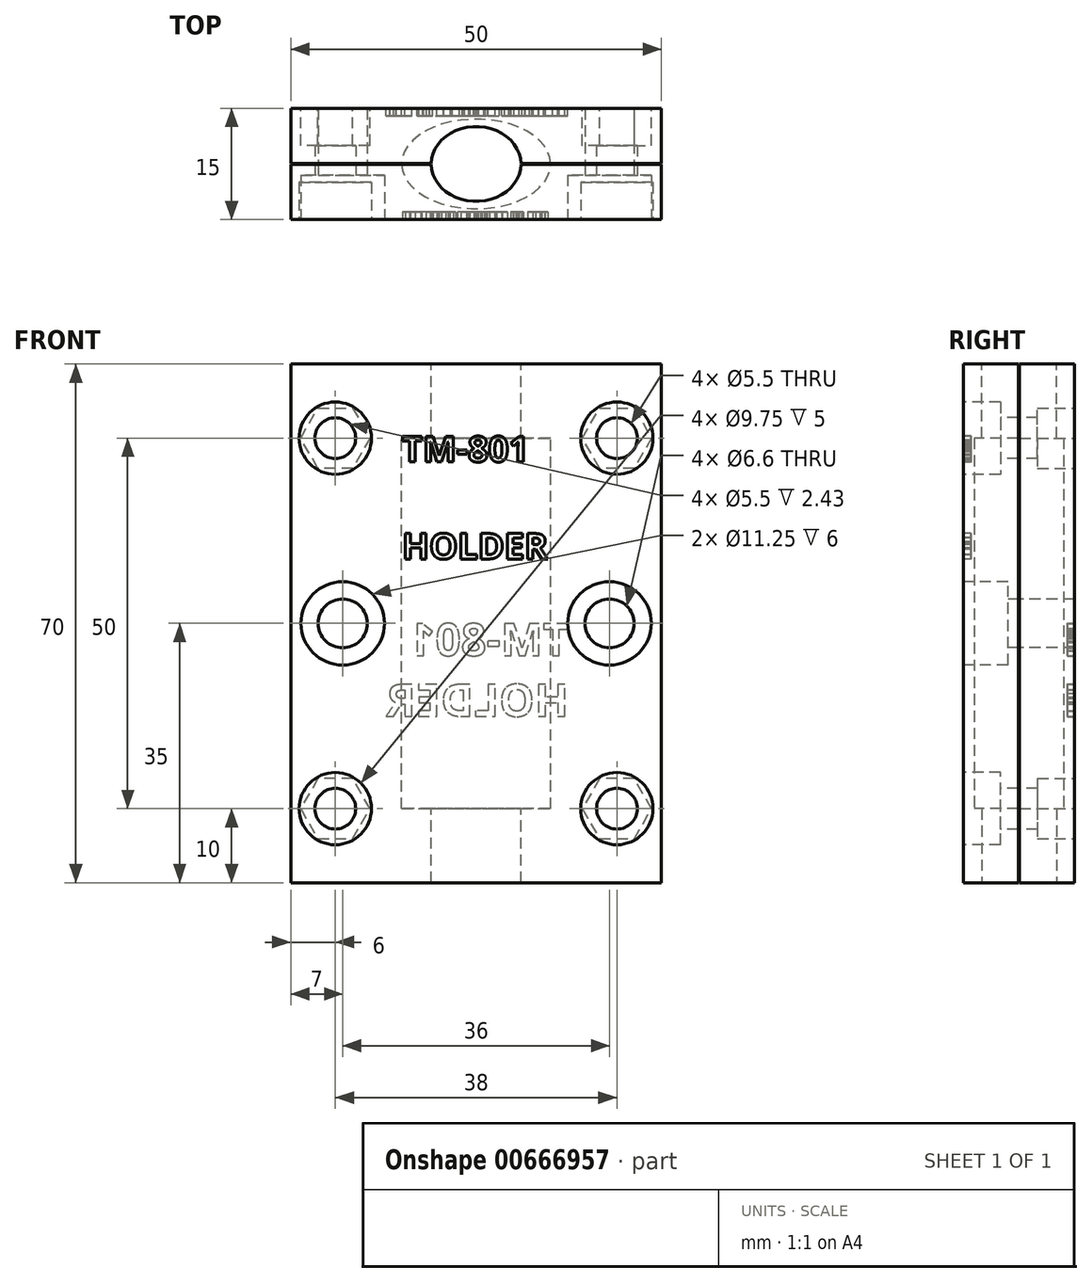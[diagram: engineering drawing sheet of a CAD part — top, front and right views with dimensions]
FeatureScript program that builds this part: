
annotation { "Feature Type Name" : "Feature", "Feature Type Description" : "" }
export const myFeature = defineFeature(function(context is Context, id is Id, definition is map)
    precondition{}
    {
        {
            var Q0;
            Q0=qCreatedBy(makeId("Top.planeOp"),FACE);
            var sketch = newSketch(context, id + "F0", { "sketchPlane" : qUnion([Q0])});
            skEllipse(sketch, "E0", {"center": v(0, 0) * mm, "majorRadius": 10.05 * mm, "minorRadius": 6.05 * mm, "majorAxis": v(-1, 0)});
            skSolve(sketch);
        }
        {
            var Q0;
            Q0=makeQuery(id+"F0.imprint","IMPRINT",FACE,{"disambiguationData":[TD([[makeQuery(id+"F0.imprint","IMPRINT",EDGE,{"derivedFrom":sQuery(id+"F0.wireOp",EDGE,"E0")}),1.0]])]});
            var sketch = newSketch(context, id + "F1", { "sketchPlane" : qUnion([Q0])});
            skEllipse(sketch, "E1", {"center": v(0, 0) * mm, "majorRadius": 6.05 * mm, "minorRadius": 5.05 * mm, "majorAxis": v(-1, 0)});
            skSolve(sketch);
        }
        {
            var Q0;
            Q0=qCreatedBy(makeId("Top.planeOp"),FACE);
            var sketch = newSketch(context, id + "F2", { "sketchPlane" : qUnion([Q0])});
            skLineSegment(sketch, "E2.bottom", {"start": v(-25, -7.5) * mm, "end": v(25, -7.5) * mm});
            skLineSegment(sketch, "E2.top", {"start": v(-25, 7.5) * mm, "end": v(25, 7.5) * mm});
            skLineSegment(sketch, "E2.left", {"start": v(-25, -7.5) * mm, "end": v(-25, 7.5) * mm});
            skLineSegment(sketch, "E2.right", {"start": v(25, -7.5) * mm, "end": v(25, 7.5) * mm});
            skPoint(sketch, "E2.middle", {"position": v(0, 0) * mm});
            skSolve(sketch);
        }
        {
            var Q0;
            Q0 = qSketchRegion(id + "F2", true);
            extrude(context, id + "F3", {"entities" : qUnion([Q0]), "oppositeDirection" : true, "depth" : 35 * mm, "offsetDistance" : 25 * mm});
        }
        {
            var Q0;
            Q0=makeQuery(id+"F1.imprint","IMPRINT",FACE,{"disambiguationData":[TD([[makeQuery(id+"F1.imprint","IMPRINT",EDGE,{"derivedFrom":sQuery(id+"F1.wireOp",EDGE,"E1")}),1.0]])]});
            var Q1;
            Q1=sQuery(id+"F1.wireOp",EDGE,"E1");
            extrude(context, id + "F4", {"entities" : qUnion([Q0]), "operationType" : NewBodyOperationType.REMOVE, "surfaceEntities" : qUnion([Q1]), "endBound" : BoundingType.THROUGH_ALL, "oppositeDirection" : true, "depth" : 25 * mm, "offsetDistance" : 25 * mm});
        }
        {
            var Q0;
            Q0 = qSketchRegion(id + "F0", true);
            var Q1;
            Q1=sQuery(id+"F0.wireOp",EDGE,"E0");
            extrude(context, id + "F5", {"entities" : qUnion([Q0]), "operationType" : NewBodyOperationType.REMOVE, "surfaceEntities" : qUnion([Q1]), "oppositeDirection" : true, "depth" : 25 * mm, "offsetDistance" : 25 * mm});
        }
        {
            var Q0;
            Q0=makeQuery(id+"F3.opExtrude","SWEPT_FACE",FACE,{"disambiguationData":[OSD([sQuery(id+"F2.wireOp",EDGE,"E2.bottom")])]});
            var sketch = newSketch(context, id + "F6", { "sketchPlane" : qUnion([Q0])});
            skPoint(sketch, "E3", {"position": v(-19, -25) * mm});
            skPoint(sketch, "E4", {"position": v(19, -25) * mm});
            skSolve(sketch);
        }
        {
            var Q0;
            Q0=sQuery(id+"F6.wireOp",VERTEX,"E3");
            var Q1;
            Q1=sQuery(id+"F6.wireOp",VERTEX,"E4");
            var Q2;
            Q2=makeQuery(id+"F3.opExtrude","SWEPT_BODY",BODY,{"disambiguationData":[OSD([sQuery(id+"F2.wireOp",EDGE,"E2.bottom"),sQuery(id+"F2.wireOp",EDGE,"E2.top"),sQuery(id+"F2.wireOp",EDGE,"E2.left"),sQuery(id+"F2.wireOp",EDGE,"E2.right")])]});
            hole(context, id + "F7", {"style" : HoleStyle.C_BORE, "endStyle" : HoleEndStyle.THROUGH, "standardTappedOrClearance" : lookupTablePath({ "standard" : "ISO", "fit" : "Normal", "size" : "M5", "type" : "Clearance" }), "standardBlindInLast" : lookupTablePath({ "fit" : "Standard", "standard" : "ISO", "size" : "M5", "type" : "Clearance" }), "holeDiameter" : 5.5 * mm, "cBoreDiameter" : 9.75 * mm, "cBoreDepth" : 5 * mm, "majorDiameter" : 5 * mm, "isTappedThrough" : true, "tappedDepth" : 12 * mm, "tapClearance" : 3, "startFromSketch" : true, "locations" : qUnion([Q0, Q1]), "scope" : qUnion([Q2])});
        }
        {
            var Q0;
            Q0=makeQuery(id+"F3.opExtrude","SWEPT_FACE",FACE,{"disambiguationData":[OSD([sQuery(id+"F2.wireOp",EDGE,"E2.top")])]});
            var sketch = newSketch(context, id + "F8", { "sketchPlane" : qUnion([Q0])});
            skCircle(sketch, "E5.cCircle", {"center": v(-19, -25) * mm, "radius": 4.05 * mm, "construction": true});
            skLineSegment(sketch, "E5.0", {"start": v(-16.66, -29.05) * mm, "end": v(-21.34, -29.05) * mm});
            skLineSegment(sketch, "E5.1", {"start": v(-21.34, -29.05) * mm, "end": v(-23.68, -25) * mm});
            skLineSegment(sketch, "E5.2", {"start": v(-23.68, -25) * mm, "end": v(-21.34, -20.95) * mm});
            skLineSegment(sketch, "E5.3", {"start": v(-21.34, -20.95) * mm, "end": v(-16.66, -20.95) * mm});
            skLineSegment(sketch, "E5.4", {"start": v(-16.66, -20.95) * mm, "end": v(-14.32, -25) * mm});
            skLineSegment(sketch, "E5.5", {"start": v(-14.32, -25) * mm, "end": v(-16.66, -29.05) * mm});
            skPoint(sketch, "E5.0.midPoint", {"position": v(-19, -29.05) * mm});
            skPoint(sketch, "E6.0.midPoint", {"position": v(-22.5, -27.03) * mm});
            skCircle(sketch, "E7.cCircle", {"center": v(19, -25) * mm, "radius": 4.05 * mm, "construction": true});
            skLineSegment(sketch, "E7.0", {"start": v(16.66, -29.05) * mm, "end": v(14.32, -25) * mm});
            skLineSegment(sketch, "E7.1", {"start": v(14.32, -25) * mm, "end": v(16.66, -20.95) * mm});
            skLineSegment(sketch, "E7.2", {"start": v(16.66, -20.95) * mm, "end": v(21.34, -20.95) * mm});
            skLineSegment(sketch, "E7.3", {"start": v(21.34, -20.95) * mm, "end": v(23.68, -25) * mm});
            skLineSegment(sketch, "E7.4", {"start": v(23.68, -25) * mm, "end": v(21.34, -29.05) * mm});
            skLineSegment(sketch, "E7.5", {"start": v(21.34, -29.05) * mm, "end": v(16.66, -29.05) * mm});
            skPoint(sketch, "E7.0.midPoint", {"position": v(15.5, -27.03) * mm});
            skSolve(sketch);
        }
        {
            var Q0;
            Q0=makeQuery(id+"F8.imprint","IMPRINT",FACE,{"disambiguationData":[TD([[makeQuery(id+"F8.imprint","IMPRINT",EDGE,{"derivedFrom":sQuery(id+"F8.wireOp",EDGE,"E5.1")}),-1.0]])]});
            extrude(context, id + "F9", {"entities" : qUnion([Q0]), "operationType" : NewBodyOperationType.REMOVE, "oppositeDirection" : true, "depth" : 5 * mm, "offsetDistance" : 25 * mm});
        }
        {
            var Q0;
            Q0 = qSketchRegion(id + "F8", true);
            extrude(context, id + "F10", {"entities" : qUnion([Q0]), "operationType" : NewBodyOperationType.REMOVE, "oppositeDirection" : true, "depth" : 5 * mm, "offsetDistance" : 25 * mm});
        }
        {
            var Q0;
            Q0=makeQuery(id+"F3.opExtrude","SWEPT_BODY",BODY,{"disambiguationData":[OSD([sQuery(id+"F2.wireOp",EDGE,"E2.bottom"),sQuery(id+"F2.wireOp",EDGE,"E2.top"),sQuery(id+"F2.wireOp",EDGE,"E2.left"),sQuery(id+"F2.wireOp",EDGE,"E2.right")])]});
            var Q1;
            Q1=makeQuery(id+"F2.imprint","IMPRINT",FACE,{"disambiguationData":[TD([[makeQuery(id+"F2.imprint","IMPRINT",EDGE,{"derivedFrom":sQuery(id+"F2.wireOp",EDGE,"E2.bottom")}),1.0]])]});
            mirror(context, id + "F11", {"operationType" : NewBodyOperationType.ADD, "entities" : qUnion([Q0]), "mirrorPlane" : qUnion([Q1])});
        }
        {
            var Q0;
            {var subQ0=makeQuery(id+"F3.opExtrude","SWEPT_FACE",FACE,{"disambiguationData":[OSD([sQuery(id+"F2.wireOp",EDGE,"E2.bottom")])]});Q0=makeQuery(id+"F11.boolean.opBoolean","MERGE",FACE,{"derivedFrom":[subQ0,makeQuery(id+"F11.opPattern","COPY",FACE,{"derivedFrom":subQ0,"instanceName":"1"})]});}
            var sketch = newSketch(context, id + "F12", { "sketchPlane" : qUnion([Q0])});
            skPoint(sketch, "E8", {"position": v(-18, 0) * mm});
            skPoint(sketch, "E9", {"position": v(18, 0) * mm});
            skSolve(sketch);
        }
        {
            var Q0;
            Q0=sQuery(id+"F12.wireOp",VERTEX,"E8");
            var Q1;
            Q1=sQuery(id+"F12.wireOp",VERTEX,"E9");
            var Q2;
            Q2=makeQuery(id+"F3.opExtrude","SWEPT_BODY",BODY,{"disambiguationData":[OSD([sQuery(id+"F2.wireOp",EDGE,"E2.bottom"),sQuery(id+"F2.wireOp",EDGE,"E2.top"),sQuery(id+"F2.wireOp",EDGE,"E2.left"),sQuery(id+"F2.wireOp",EDGE,"E2.right")])]});
            hole(context, id + "F13", {"style" : HoleStyle.C_BORE, "endStyle" : HoleEndStyle.THROUGH, "standardTappedOrClearance" : lookupTablePath({ "standard" : "ISO", "fit" : "Normal", "size" : "M6", "type" : "Clearance" }), "standardBlindInLast" : lookupTablePath({ "fit" : "Standard", "standard" : "ISO", "size" : "M6", "type" : "Clearance" }), "holeDiameter" : 6.6 * mm, "cBoreDiameter" : 11.25 * mm, "cBoreDepth" : 6 * mm, "majorDiameter" : 5 * mm, "isTappedThrough" : true, "tappedDepth" : 12 * mm, "tapClearance" : 3, "startFromSketch" : true, "locations" : qUnion([Q0, Q1]), "scope" : qUnion([Q2])});
        }
        {
            var Q0;
            Q0=makeQuery(id+"F11.opPattern","COPY",FACE,{"derivedFrom":makeQuery(id+"F3.opExtrude","CAP_FACE",FACE,{"disambiguationData":[OSD([sQuery(id+"F2.wireOp",EDGE,"E2.bottom"),sQuery(id+"F2.wireOp",EDGE,"E2.top"),sQuery(id+"F2.wireOp",EDGE,"E2.left"),sQuery(id+"F2.wireOp",EDGE,"E2.right")])],"isStart":false}),"instanceName":"1"});
            var sketch = newSketch(context, id + "F14", { "sketchPlane" : qUnion([Q0])});
            skLineSegment(sketch, "E10.bottom", {"start": v(-25, -0.08) * mm, "end": v(25, -0.08) * mm});
            skLineSegment(sketch, "E10.top", {"start": v(-25, 0.07) * mm, "end": v(25, 0.07) * mm});
            skLineSegment(sketch, "E10.left", {"start": v(-25, -0.07) * mm, "end": v(-25, 0.08) * mm});
            skLineSegment(sketch, "E10.right", {"start": v(25, -0.07) * mm, "end": v(25, 0.08) * mm});
            skPoint(sketch, "E10.middle", {"position": v(0, 0) * mm});
            skSolve(sketch);
        }
        {
            var Q0;
            {var subQ0=sQuery(id+"F14.wireOp",EDGE,"E10.left");Q0=makeQuery(id+"F14.imprint","IMPRINT",FACE,{"disambiguationData":[TD([[makeQuery(id+"F14.imprint","IMPRINT",EDGE,{"derivedFrom":subQ0}),-1.0]])]});}
            var Q1;
            {var subQ0=sQuery(id+"F14.wireOp",EDGE,"E10.right");Q1=makeQuery(id+"F14.imprint","IMPRINT",FACE,{"disambiguationData":[TD([[makeQuery(id+"F14.imprint","IMPRINT",EDGE,{"derivedFrom":subQ0}),1.0]])]});}
            extrude(context, id + "F15", {"entities" : qUnion([Q0, Q1]), "operationType" : NewBodyOperationType.REMOVE, "endBound" : BoundingType.THROUGH_ALL, "oppositeDirection" : true, "depth" : 25 * mm, "offsetDistance" : 25 * mm});
        }
        {
            var Q0;
            {var subQ0=makeQuery(id+"F3.opExtrude","SWEPT_FACE",FACE,{"disambiguationData":[OSD([sQuery(id+"F2.wireOp",EDGE,"E2.bottom")])]});Q0=makeQuery(id+"F11.boolean.opBoolean","MERGE",FACE,{"derivedFrom":[subQ0,makeQuery(id+"F11.opPattern","COPY",FACE,{"derivedFrom":subQ0,"instanceName":"1"})]});}
            var sketch = newSketch(context, id + "F16", { "sketchPlane" : qUnion([Q0])});
            skText(sketch, "E11", { "text": "TM-801\n\nHOLDER", "fontName": "OpenSans-Bold.ttf"});
            const initialGuessF16  = {"E11": [-0.01, 0.0218, 1, 0, 0.00347]};
            skSetInitialGuess(sketch, initialGuessF16);
            skSolve(sketch);
        }
        {
            var Q0;
            Q0 = qSketchRegion(id + "F16", true);
            extrude(context, id + "F17", {"entities" : qUnion([Q0]), "operationType" : NewBodyOperationType.REMOVE, "oppositeDirection" : true, "depth" : 1 * mm, "offsetDistance" : 25 * mm});
        }
        {
            var Q0;
            {var subQ0=makeQuery(id+"F3.opExtrude","SWEPT_FACE",FACE,{"disambiguationData":[OSD([sQuery(id+"F2.wireOp",EDGE,"E2.top")])]});Q0=makeQuery(id+"F11.boolean.opBoolean","MERGE",FACE,{"derivedFrom":[subQ0,makeQuery(id+"F11.opPattern","COPY",FACE,{"derivedFrom":subQ0,"instanceName":"1"})]});}
            var sketch = newSketch(context, id + "F18", { "sketchPlane" : qUnion([Q0])});
            skText(sketch, "E12", { "text": "TM-801\nHOLDER", "fontName": "OpenSans-Bold.ttf"});
            const initialGuessF18  = {"E12": [-0.0125, -0.00434, 1, 0, 0.00434]};
            skSetInitialGuess(sketch, initialGuessF18);
            skSolve(sketch);
        }
        {
            var Q0;
            Q0 = qSketchRegion(id + "F18", true);
            extrude(context, id + "F19", {"entities" : qUnion([Q0]), "operationType" : NewBodyOperationType.REMOVE, "oppositeDirection" : true, "depth" : 1 * mm, "offsetDistance" : 25 * mm});
        }
    });
